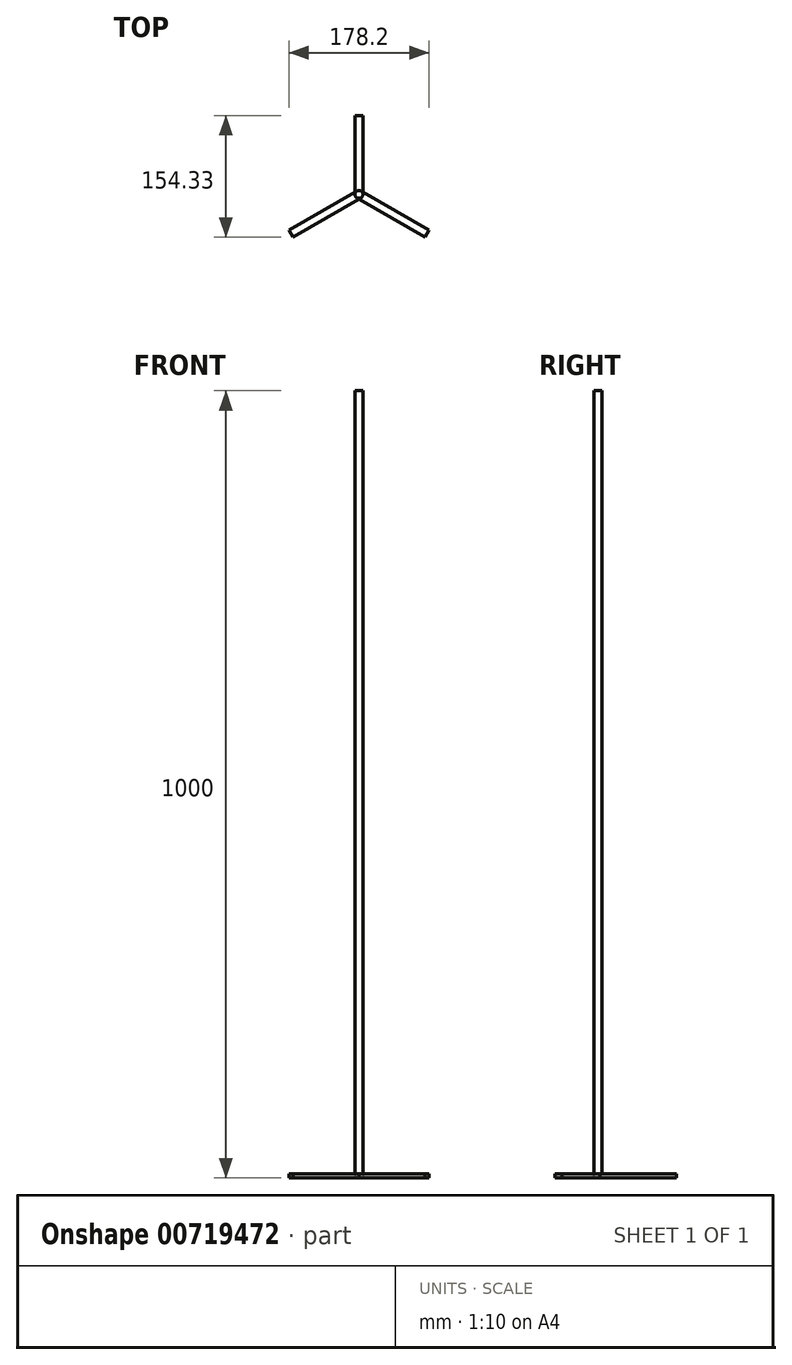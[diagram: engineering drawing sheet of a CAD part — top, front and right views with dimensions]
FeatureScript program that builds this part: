
annotation { "Feature Type Name" : "Feature", "Feature Type Description" : "" }
export const myFeature = defineFeature(function(context is Context, id is Id, definition is map)
    precondition{}
    {
        {
            var Q0;
            Q0=qCreatedBy(makeId("Top.planeOp"),FACE);
            var sketch = newSketch(context, id + "F0", { "sketchPlane" : qUnion([Q0])});
            skLineSegment(sketch, "E0", {"start": v(0, 0) * mm, "end": v(-86.6, -50) * mm, "construction": true});
            skLineSegment(sketch, "E1", {"start": v(0, 0) * mm, "end": v(86.6, -50) * mm, "construction": true});
            skLineSegment(sketch, "E2", {"start": v(0, 0) * mm, "end": v(0, 100) * mm, "construction": true});
            skLineSegment(sketch, "E3", {"start": v(-86.6, -50) * mm, "end": v(-89.1, -45.67) * mm});
            skLineSegment(sketch, "E4", {"start": v(-89.1, -45.67) * mm, "end": v(-2.5, 4.33) * mm});
            skLineSegment(sketch, "E5.MirrorCS", {"start": v(-84.1, -54.33) * mm, "end": v(2.5, -4.33) * mm});
            skLineSegment(sketch, "E6.MirrorCS", {"start": v(-86.6, -50) * mm, "end": v(-84.1, -54.33) * mm});
            skLineSegment(sketch, "E7", {"start": v(-2.5, 4.33) * mm, "end": v(2.5, -4.33) * mm});
            skLineSegment(sketch, "E8.MirrorCS", {"start": v(89.1, -45.67) * mm, "end": v(2.5, 4.33) * mm});
            skLineSegment(sketch, "E9.MirrorCS", {"start": v(2.5, 4.33) * mm, "end": v(-2.5, -4.33) * mm});
            skLineSegment(sketch, "E10.MirrorCS", {"start": v(84.1, -54.33) * mm, "end": v(-2.5, -4.33) * mm});
            skLineSegment(sketch, "E11.MirrorCS", {"start": v(86.6, -50) * mm, "end": v(84.1, -54.33) * mm});
            skLineSegment(sketch, "E12.MirrorCS", {"start": v(86.6, -50) * mm, "end": v(89.1, -45.67) * mm});
            skLineSegment(sketch, "E13.bottom", {"start": v(5, 100) * mm, "end": v(-5, 100) * mm});
            skLineSegment(sketch, "E13.top", {"start": v(5, 0) * mm, "end": v(-5, 0) * mm});
            skLineSegment(sketch, "E13.left", {"start": v(5, 100) * mm, "end": v(5, 0) * mm});
            skLineSegment(sketch, "E13.right", {"start": v(-5, 100) * mm, "end": v(-5, 0) * mm});
            skPoint(sketch, "E13.middle", {"position": v(0, 50) * mm});
            skCircle(sketch, "E14", {"center": v(0, 0) * mm, "radius": 5 * mm});
            skSolve(sketch);
        }
        {
            var Q0;
            {var subQ0=sQuery(id+"F0.wireOp",EDGE,"E13.bottom");Q0=makeQuery(id+"F0.imprint","IMPRINT",FACE,{"disambiguationData":[TD([[makeQuery(id+"F0.imprint","IMPRINT",EDGE,{"derivedFrom":subQ0}),1.0]])]});}
            var Q1;
            {var subQ1=sQuery(id+"F0.wireOp",EDGE,"E4");var subQ3=sQuery(id+"F0.wireOp",EDGE,"E13.right");var subQ4=makeQuery(id+"F0.imprint","INTERSECT",VERTEX,{"derivedFrom":[subQ1,subQ3]});Q1=makeQuery(id+"F0.imprint","IMPRINT",FACE,{"disambiguationData":[TD([[makeQuery(id+"F0.imprint","IMPRINT",EDGE,{"disambiguationData":[TD([[subQ4,-1.0]])],"derivedFrom":subQ1}),-1.0]])]});}
            var Q2;
            {var subQ5=sQuery(id+"F0.wireOp",EDGE,"E3");Q2=makeQuery(id+"F0.imprint","IMPRINT",FACE,{"disambiguationData":[TD([[makeQuery(id+"F0.imprint","IMPRINT",EDGE,{"derivedFrom":subQ5}),-1.0]])]});}
            var Q3;
            {var subQ1=sQuery(id+"F0.wireOp",EDGE,"E5.MirrorCS");var subQ3=sQuery(id+"F0.wireOp",EDGE,"E10.MirrorCS");var subQ4=makeQuery(id+"F0.imprint","INTERSECT",VERTEX,{"derivedFrom":[subQ1,subQ3]});Q3=makeQuery(id+"F0.imprint","IMPRINT",FACE,{"disambiguationData":[TD([[makeQuery(id+"F0.imprint","IMPRINT",EDGE,{"disambiguationData":[TD([[subQ4,-1.0]])],"derivedFrom":subQ1}),1.0]])]});}
            var Q4;
            {var subQ0=sQuery(id+"F0.wireOp",EDGE,"E11.MirrorCS");Q4=makeQuery(id+"F0.imprint","IMPRINT",FACE,{"disambiguationData":[TD([[makeQuery(id+"F0.imprint","IMPRINT",EDGE,{"derivedFrom":subQ0}),-1.0]])]});}
            var Q5;
            {var subQ1=sQuery(id+"F0.wireOp",EDGE,"E8.MirrorCS");var subQ3=sQuery(id+"F0.wireOp",EDGE,"E13.left");var subQ4=makeQuery(id+"F0.imprint","INTERSECT",VERTEX,{"derivedFrom":[subQ1,subQ3]});Q5=makeQuery(id+"F0.imprint","IMPRINT",FACE,{"disambiguationData":[TD([[makeQuery(id+"F0.imprint","IMPRINT",EDGE,{"disambiguationData":[TD([[subQ4,-1.0]])],"derivedFrom":subQ1}),1.0]])]});}
            extrude(context, id + "F1", {"entities" : qUnion([Q0, Q1, Q2, Q3, Q4, Q5]), "depth" : 5 * mm, "offsetDistance" : 25 * mm});
        }
        {
            var Q0;
            {var subQ0=sQuery(id+"F0.wireOp",EDGE,"E14");var subQ1=sQuery(id+"F0.wireOp",EDGE,"E9.MirrorCS");var subQ2=makeQuery(id+"F0.imprint","INTERSECT",VERTEX,{"derivedFrom":[sQuery(id+"F0.wireOp",EDGE,"E8.MirrorCS"),subQ1,subQ0]});Q0=makeQuery(id+"F0.imprint","IMPRINT",FACE,{"disambiguationData":[TD([[makeQuery(id+"F0.imprint","IMPRINT",EDGE,{"disambiguationData":[TD([[subQ2,-1.0]])],"derivedFrom":subQ1}),1.0]])]});}
            var Q1;
            {var subQ0=sQuery(id+"F0.wireOp",EDGE,"E14");var subQ1=sQuery(id+"F0.wireOp",EDGE,"E7");var subQ2=makeQuery(id+"F0.imprint","INTERSECT",VERTEX,{"derivedFrom":[sQuery(id+"F0.wireOp",EDGE,"E5.MirrorCS"),subQ1,subQ0]});Q1=makeQuery(id+"F0.imprint","IMPRINT",FACE,{"disambiguationData":[TD([[makeQuery(id+"F0.imprint","IMPRINT",EDGE,{"disambiguationData":[TD([[subQ2,1.0]])],"derivedFrom":subQ1}),1.0]])]});}
            var Q2;
            {var subQ0=sQuery(id+"F0.wireOp",EDGE,"E14");var subQ1=sQuery(id+"F0.wireOp",EDGE,"E7");var subQ2=makeQuery(id+"F0.imprint","INTERSECT",VERTEX,{"derivedFrom":[sQuery(id+"F0.wireOp",EDGE,"E5.MirrorCS"),subQ1,subQ0]});Q2=makeQuery(id+"F0.imprint","IMPRINT",FACE,{"disambiguationData":[TD([[makeQuery(id+"F0.imprint","IMPRINT",EDGE,{"disambiguationData":[TD([[subQ2,1.0]])],"derivedFrom":subQ1}),-1.0]])]});}
            var Q3;
            {var subQ0=sQuery(id+"F0.wireOp",EDGE,"E14");var subQ1=sQuery(id+"F0.wireOp",EDGE,"E9.MirrorCS");var subQ2=makeQuery(id+"F0.imprint","INTERSECT",VERTEX,{"derivedFrom":[subQ1,sQuery(id+"F0.wireOp",EDGE,"E10.MirrorCS"),subQ0]});Q3=makeQuery(id+"F0.imprint","IMPRINT",FACE,{"disambiguationData":[TD([[makeQuery(id+"F0.imprint","IMPRINT",EDGE,{"disambiguationData":[TD([[subQ2,1.0]])],"derivedFrom":subQ1}),-1.0]])]});}
            var Q4;
            {var subQ0=sQuery(id+"F0.wireOp",EDGE,"E14");var subQ1=sQuery(id+"F0.wireOp",EDGE,"E7");var subQ2=makeQuery(id+"F0.imprint","INTERSECT",VERTEX,{"derivedFrom":[sQuery(id+"F0.wireOp",EDGE,"E4"),subQ1,subQ0]});Q4=makeQuery(id+"F0.imprint","IMPRINT",FACE,{"disambiguationData":[TD([[makeQuery(id+"F0.imprint","IMPRINT",EDGE,{"disambiguationData":[TD([[subQ2,-1.0]])],"derivedFrom":subQ1}),-1.0]])]});}
            var Q5;
            {var subQ0=sQuery(id+"F0.wireOp",EDGE,"E14");var subQ1=sQuery(id+"F0.wireOp",EDGE,"E7");var subQ2=makeQuery(id+"F0.imprint","INTERSECT",VERTEX,{"derivedFrom":[sQuery(id+"F0.wireOp",EDGE,"E4"),subQ1,subQ0]});Q5=makeQuery(id+"F0.imprint","IMPRINT",FACE,{"disambiguationData":[TD([[makeQuery(id+"F0.imprint","IMPRINT",EDGE,{"disambiguationData":[TD([[subQ2,-1.0]])],"derivedFrom":subQ1}),1.0]])]});}
            extrude(context, id + "F2", {"entities" : qUnion([Q0, Q1, Q2, Q3, Q4, Q5]), "operationType" : NewBodyOperationType.ADD, "depth" : 1000 * mm, "offsetDistance" : 25 * mm});
        }
    });
